# Revit family: 2049519 Lighting Fixture_Sylvania_Myriad V LED_Ceiling Recessed
name_source: partatom
category: Lighting Fixtures
revit_build: Autodesk Revit 2015 (Build: 20140606_1530(x64)
units: mm (PartAtom-declared; Revit-internal decimal feet)

## types (1)
- MYRIAD SS HOUS 3000K DALI
    Apparent Load = 15 VA
    Assembly Code = D5020200
    Beam Angle = 30.00°
    Body Material = Aluminum_Sylvania_Myrad V LED_Silver
    Color Filter = 16777215
    Cutout Diameter = 75 mm
    Cutout Radius = 37.5 mm
    Default Elevation = 0 mm  [stored 0 ft]
    Description = New high output high efficiency LED downlight modules. IR/UV free light source without heat radiation. Energy efficient light source with far superior luminous flux per watt than existing Low Voltage Halogen. Long life up to 50K hours, fit and forget maintenance free lighting solution. Dimmable options including DALI as standard. IP44 & IP65 versions as standard options. New range of Architectural accessories each providing a different lit dimension. Choice of colour temperatures warm 3000K and neutral 4000K. Luminaires supplied complete with LED drivers. Emergency versions passes through cut out. New completely flush plaster up accessory ring for clean ceiling lines and smooth finish. Total circuit power I5W
    Diffuser Diameter = 77 mm  [stored 0.252625 ft]
    Diffuser Material = Polycarbonate_Sylvania_Myrad V LED_Clear
    Dimming Lamp Color Temperature Shift = <None>
    Electrical Protection = CLASS II
    Emit Shape Visible in Rendering = No
    Emit from Circle Diameter = 77 mm  [stored 0.252625 ft]
    Height = 72 mm  [stored 0.23622 ft]
    IP Rating = IP20/44(with accessories)
    Inner Radius = 35.5 mm  [stored 0.11647 ft]
    LOR = 100%
    Lamp = Integrated LED
    Lamp Comments = 15W Citizen Citiled neutral 4000K
    Life = 50 000
    Manufacturer = Feilo-Sylvania Group
    Model = 2049519 MYRIAD SS HOUS 3000K ELEC
    Photometric Web File = 2049519_MYRIADVLED16W3KDALI-90256.ies
    Product Family = MYRIAD V LED - HOUSING ONLY
    Recessed Depth = 72 mm  [stored 0.23622 ft]
    Reflector Material = Steel_Sylvania_Myrad V LED_Chrome
    Tilt Angle = -90.00°
    Voltage = 240 V
    Voltage Comments = UNV (Universal Voltage; 220-240 Volt)
    Weight = 0.37 kg

note: [stored X ft] marks values corroborated as IEEE doubles in the binary element streams (Revit-internal decimal feet)

## geometry (parser evidence)
native form markers: Blend x7, Sweep x2
no freeform markers — native parametric forms only
